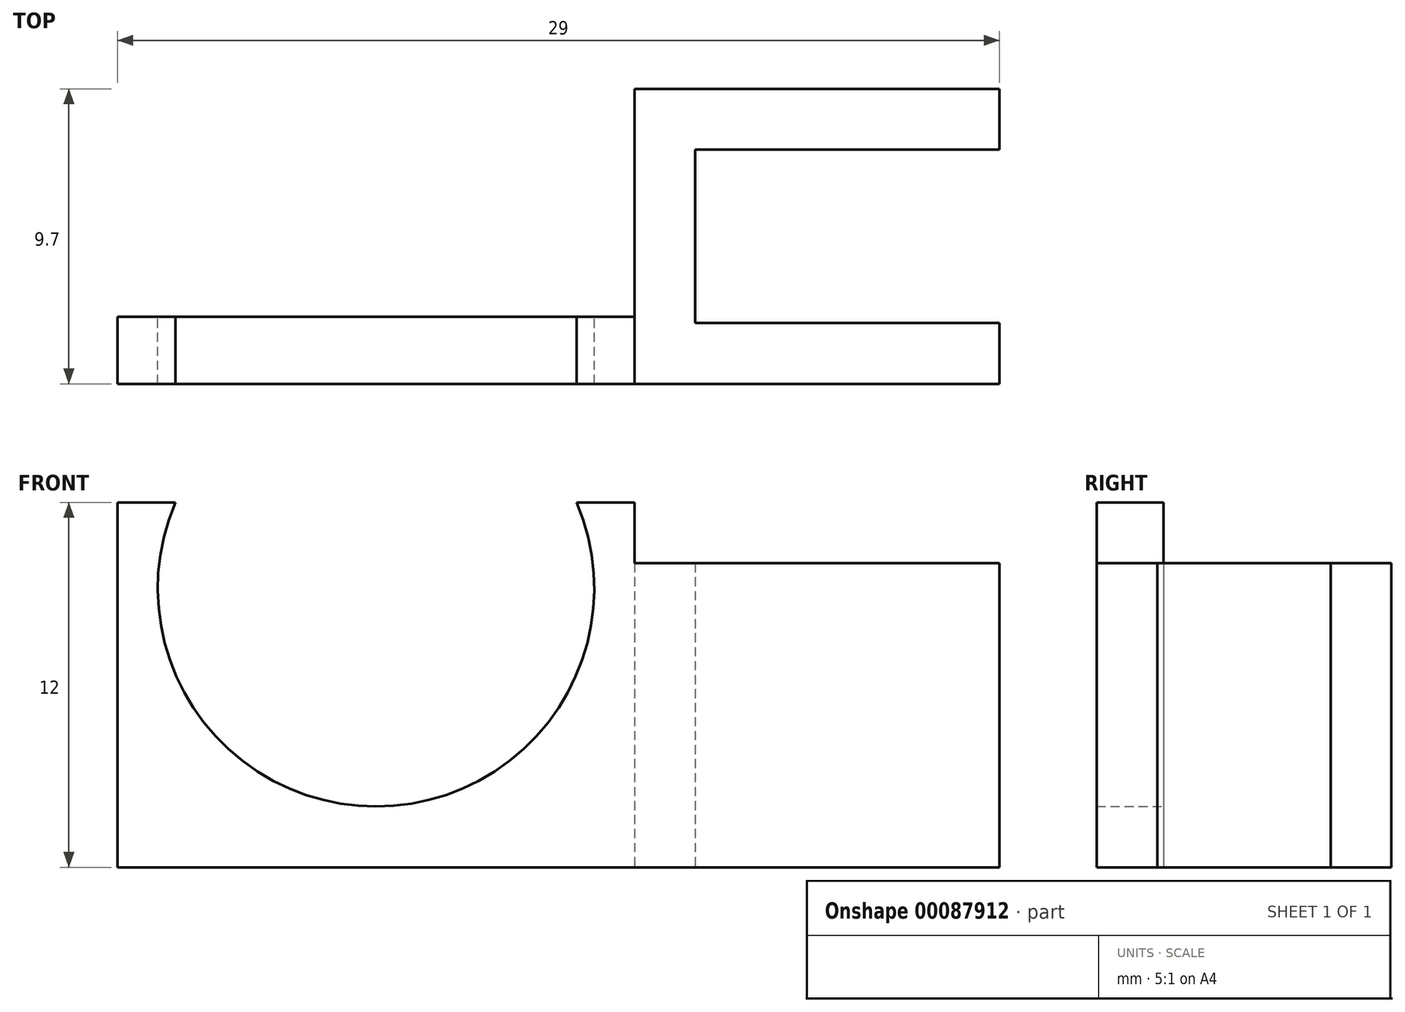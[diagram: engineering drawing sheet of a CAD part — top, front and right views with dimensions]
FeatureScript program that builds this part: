
annotation { "Feature Type Name" : "Feature", "Feature Type Description" : "" }
export const myFeature = defineFeature(function(context is Context, id is Id, definition is map)
    precondition{}
    {
        {
            var Q0;
            Q0=qCreatedBy(makeId("Top.planeOp"),FACE);
            var sketch = newSketch(context, id + "F0", { "sketchPlane" : qUnion([Q0])});
            skLineSegment(sketch, "E0.bottom", {"start": v(2, 0) * mm, "end": v(10, 0) * mm});
            skLineSegment(sketch, "E0.top", {"start": v(0, 2) * mm, "end": v(10, 2) * mm});
            skLineSegment(sketch, "E0.left", {"start": v(0, 0) * mm, "end": v(0, 2) * mm});
            skLineSegment(sketch, "E1.left", {"start": v(0, 0) * mm, "end": v(0, -5.7) * mm});
            skLineSegment(sketch, "E1.right", {"start": v(2, 0) * mm, "end": v(2, -5.7) * mm});
            skLineSegment(sketch, "E2.bottom", {"start": v(2, -5.7) * mm, "end": v(10, -5.7) * mm});
            skLineSegment(sketch, "E2.top", {"start": v(0, -7.7) * mm, "end": v(10, -7.7) * mm});
            skLineSegment(sketch, "E3.left", {"start": v(0, 2) * mm, "end": v(0, -5.7) * mm});
            skLineSegment(sketch, "E4.bottom", {"start": v(0, -7.7) * mm, "end": v(-10, -7.7) * mm});
            skLineSegment(sketch, "E4.top", {"start": v(3.46, -5.5) * mm, "end": v(-7.94, -5.5) * mm});
            skLineSegment(sketch, "E5", {"start": v(-7.94, -5.5) * mm, "end": v(-13.94, -5.5) * mm});
            skLineSegment(sketch, "E6", {"start": v(-15, -7.7) * mm, "end": v(-7.94, -7.7) * mm});
            skLineSegment(sketch, "E7", {"start": v(-13.94, -5.5) * mm, "end": v(-16, -5.5) * mm});
            skLineSegment(sketch, "E8", {"start": v(-16, -7.7) * mm, "end": v(-15, -7.7) * mm});
            skLineSegment(sketch, "E9", {"start": v(-10, -7.7) * mm, "end": v(-7.94, -7.7) * mm});
            skLineSegment(sketch, "E10", {"start": v(-16, -5.5) * mm, "end": v(-17, -5.5) * mm});
            skLineSegment(sketch, "E11", {"start": v(-17, -5.5) * mm, "end": v(-17, -7.7) * mm});
            skLineSegment(sketch, "E12", {"start": v(-17, -7.7) * mm, "end": v(-16, -7.7) * mm});
            skLineSegment(sketch, "E13.bottom", {"start": v(10, 2) * mm, "end": v(12, 2) * mm});
            skLineSegment(sketch, "E13.top", {"start": v(10, 0) * mm, "end": v(12, 0) * mm});
            skLineSegment(sketch, "E13.right", {"start": v(12, 2) * mm, "end": v(12, 0) * mm});
            skLineSegment(sketch, "E14.bottom", {"start": v(10, -5.7) * mm, "end": v(12, -5.7) * mm});
            skLineSegment(sketch, "E14.top", {"start": v(10, -7.7) * mm, "end": v(12, -7.7) * mm});
            skLineSegment(sketch, "E14.right", {"start": v(12, -5.7) * mm, "end": v(12, -7.7) * mm});
            skLineSegment(sketch, "E15", {"start": v(0, -5.7) * mm, "end": v(0, -7.7) * mm});
            skSolve(sketch);
        }
        {
            var Q0;
            Q0=makeQuery(id+"F0.imprint","IMPRINT",FACE,{"disambiguationData":[TD([[makeQuery(id+"F0.imprint","IMPRINT",EDGE,{"derivedFrom":sQuery(id+"F0.wireOp",EDGE,"E0.bottom")}),1.0]])]});
            var Q1;
            {var subQ4=sQuery(id+"F0.wireOp",EDGE,"E2.bottom");Q1=makeQuery(id+"F0.imprint","IMPRINT",FACE,{"disambiguationData":[TD([[makeQuery(id+"F0.imprint","IMPRINT",EDGE,{"derivedFrom":subQ4}),-1.0]])]});}
            extrude(context, id + "F1", {"entities" : qUnion([Q0, Q1]), "depth" : 10 * mm});
        }
        {
            var Q0;
            Q0=makeQuery(id+"F0.imprint","IMPRINT",FACE,{"disambiguationData":[TD([[makeQuery(id+"F0.imprint","IMPRINT",EDGE,{"derivedFrom":sQuery(id+"F0.wireOp",EDGE,"E4.bottom")}),-1.0]])]});
            extrude(context, id + "F2", {"entities" : qUnion([Q0]), "operationType" : NewBodyOperationType.ADD, "depth" : 12 * mm});
        }
        {
            var Q0;
            Q0=makeQuery(id+"F2.opExtrude","SWEPT_FACE",FACE,{"disambiguationData":[OSD([sQuery(id+"F0.wireOp",EDGE,"E4.top"),sQuery(id+"F0.wireOp",EDGE,"E5"),sQuery(id+"F0.wireOp",EDGE,"E7"),sQuery(id+"F0.wireOp",EDGE,"E10")])]});
            var sketch = newSketch(context, id + "F3", { "sketchPlane" : qUnion([Q0])});
            skCircle(sketch, "E16", {"center": v(8.5, 9.18) * mm, "radius": 7.18 * mm});
            skLineSegment(sketch, "E17", {"start": v(0, 10.58) * mm, "end": v(17, 10.58) * mm, "construction": true});
            skPoint(sketch, "E18", {"position": v(8.5, 10.58) * mm});
            skSolve(sketch);
        }
        {
            var Q0;
            Q0=makeQuery(id+"F3.imprint","IMPRINT",FACE,{"disambiguationData":[TD([[makeQuery(id+"F3.imprint","IMPRINT",EDGE,{"derivedFrom":sQuery(id+"F3.wireOp",EDGE,"E16")}),1.0]])]});
            extrude(context, id + "F4", {"entities" : qUnion([Q0]), "operationType" : NewBodyOperationType.REMOVE, "oppositeDirection" : true, "depth" : 25 * mm});
        }
    });
